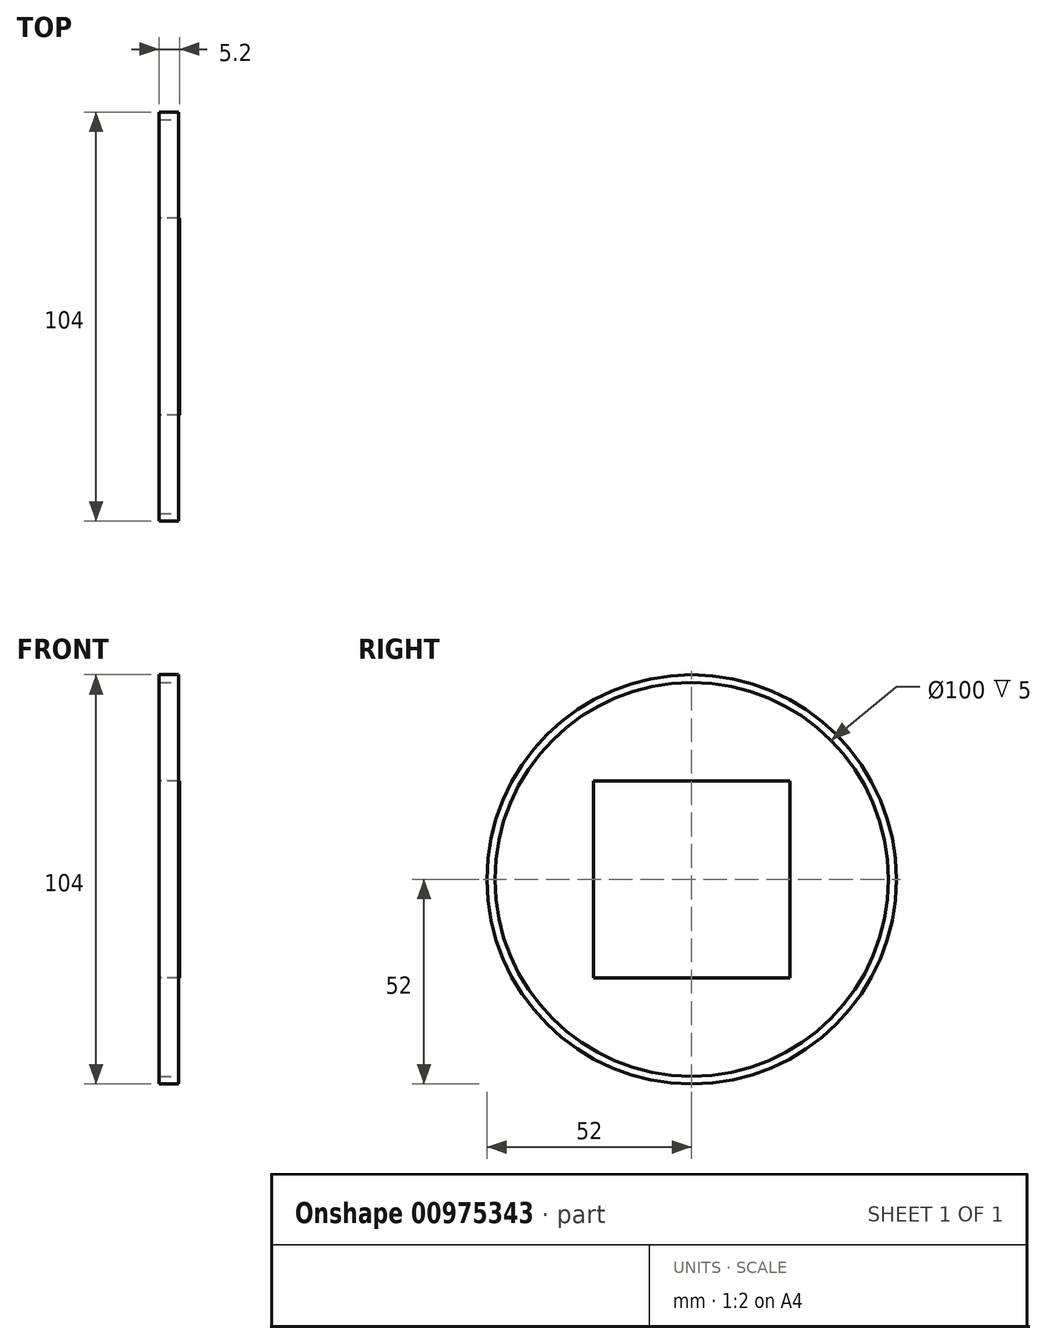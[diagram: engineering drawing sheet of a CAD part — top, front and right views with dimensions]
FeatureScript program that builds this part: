
annotation { "Feature Type Name" : "Feature", "Feature Type Description" : "" }
export const myFeature = defineFeature(function(context is Context, id is Id, definition is map)
    precondition{}
    {
        {
            var Q0;
            Q0=qCreatedBy(makeId("Front.planeOp"),FACE);
            var sketch = newSketch(context, id + "F0", { "sketchPlane" : qUnion([Q0])});
            skLineSegment(sketch, "E0", {"start": v(0, 0) * mm, "end": v(-79.76, 0) * mm, "construction": true});
            skLineSegment(sketch, "E1", {"start": v(0, 52) * mm, "end": v(-5, 52) * mm});
            skLineSegment(sketch, "E2", {"start": v(-5, 52) * mm, "end": v(-5, 50) * mm});
            skLineSegment(sketch, "E3", {"start": v(-5, 50) * mm, "end": v(0, 50) * mm});
            skLineSegment(sketch, "E4", {"start": v(0, 50) * mm, "end": v(0, 52) * mm});
            skSolve(sketch);
        }
        {
            var Q0;
            Q0=qSketchRegion(id+"F0",true);
            var Q1;
            Q1=sQuery(id+"F0.wireOp",EDGE,"E0");
            revolve(context, id + "F1", {"surfaceOperationType" : NewSurfaceOperationType.NEW, "entities" : qUnion([Q0]), "axis" : qUnion([Q1]), "revolveType" : RevolveType.FULL});
        }
        {
            var Q0;
            Q0=qCreatedBy(makeId("Right.planeOp"),FACE);
            var sketch = newSketch(context, id + "F2", { "sketchPlane" : qUnion([Q0])});
            skLineSegment(sketch, "E5.bottom", {"start": v(-25, 25) * mm, "end": v(25, 25) * mm});
            skLineSegment(sketch, "E5.top", {"start": v(-25, -25) * mm, "end": v(25, -25) * mm});
            skLineSegment(sketch, "E5.left", {"start": v(-25, 25) * mm, "end": v(-25, -25) * mm});
            skLineSegment(sketch, "E5.right", {"start": v(25, 25) * mm, "end": v(25, -25) * mm});
            skSolve(sketch);
        }
        {
            var Q0;
            Q0=makeQuery(id+"F2.imprint","IMPRINT",FACE,{"disambiguationData":[TD([[makeQuery(id+"F2.imprint","IMPRINT",EDGE,{"derivedFrom":sQuery(id+"F2.wireOp",EDGE,"E5.bottom")}),-1.0]])]});
            extrude(context, id + "F3", {"entities" : qUnion([Q0]), "depth" : 0.2 * mm, "offsetDistance" : 25 * mm, "hasSecondDirection" : true, "secondDirectionOppositeDirection" : true, "secondDirectionDepth" : 5 * mm});
        }
    });
